FCSTD DOCUMENT  (FreeCAD 0.17R13541 (Git))
Label: Acry-Base-12-10mm-slot
License: All rights reserved
LicenseURL: http://en.wikipedia.org/wiki/All_rights_reserved
objects: Sketcher::SketchObject×1, PartDesign::Body×1, App::Part×1
note: 2 computed .brp shape members not serialized (recipe doc carries the construction recipe); baked Part::Feature solids carry a one-line shape summary decoded from their .brp

FEATURE [Sketcher::SketchObject] Sketch
  MapMode = 5
  Support = -> [XY_Plane001]
  sketch-geometry (9):
    g0: ArcOfCircle CenterX=-100 CenterY=0 CenterZ=0 NormalX=0 NormalY=0 NormalZ=1 AngleXU=0 Radius=45 StartAngle=1.5708 EndAngle=4.71239
    g1: ArcOfCircle CenterX=100 CenterY=0 CenterZ=0 NormalX=0 NormalY=0 NormalZ=1 AngleXU=0 Radius=45 StartAngle=4.71239 EndAngle=7.85398
    g2: LineSegment StartX=-100 StartY=-45 StartZ=0 EndX=100 EndY=-45 EndZ=0
    g3: LineSegment StartX=-100 StartY=45 StartZ=0 EndX=100 EndY=45 EndZ=0
    g4: GeomPoint X=0 Y=-45 Z=0
    g5: ArcOfCircle CenterX=-100 CenterY=0 CenterZ=0 NormalX=0 NormalY=0 NormalZ=1 AngleXU=0 Radius=5 StartAngle=1.5708 EndAngle=4.71239
    g6: ArcOfCircle CenterX=100 CenterY=0 CenterZ=0 NormalX=0 NormalY=0 NormalZ=1 AngleXU=0 Radius=5 StartAngle=4.71239 EndAngle=7.85398
    g7: LineSegment StartX=-100 StartY=-5 StartZ=0 EndX=100 EndY=-5 EndZ=0
    g8: LineSegment StartX=-100 StartY=5 StartZ=0 EndX=100 EndY=5 EndZ=0
  constraints (21):
    c: Tangent(g0,g3) = 1.5708
    c: Tangent(g0,g2) = -1.5708
    c: Tangent(g2,g1) = -1.5708
    c: Tangent(g3,g1) = 1.5708
    c: Horizontal(g2)
    c: Equal(g0,g1)
    c: Distance(g1,g0) = 200
    c: Distance(g1,g1) = 45
    c: PointOnObject(g4,g2)
    c: Symmetric(g1,g0,g4)
    c: PointOnObject(g4,g-2)
    c: PointOnObject(g0,g-1)
    c: Tangent(g5,g8) = 1.5708
    c: Tangent(g5,g7) = -1.5708
    c: Tangent(g7,g6) = -1.5708
    c: Tangent(g8,g6) = 1.5708
    c: Horizontal(g7)
    c: Equal(g5,g6)
    c: Distance(g6,g6) = 10
    c: Coincident(g5,g0)
    c: Coincident(g6,g1)
FEATURE [PartDesign::Body] Body
  Group = -> [Sketch]
  Origin = -> Origin001
FEATURE [App::Part] Part
  Group = -> [Body]
  License = CC BY 3.0
  LicenseURL = http://creativecommons.org/licenses/by/3.0/
  Origin = -> Origin
